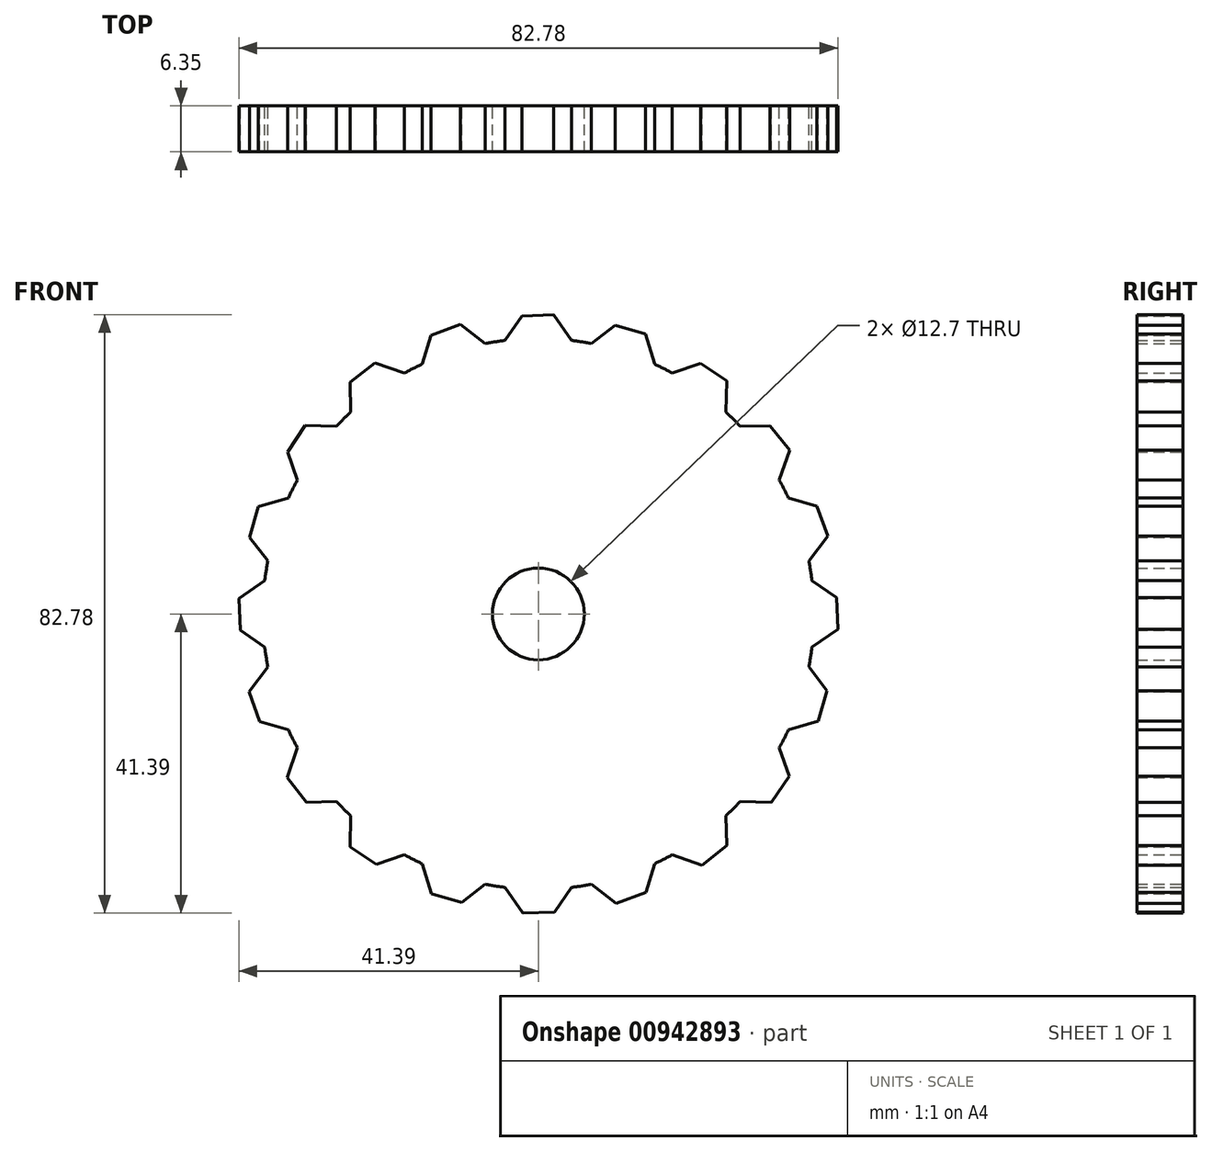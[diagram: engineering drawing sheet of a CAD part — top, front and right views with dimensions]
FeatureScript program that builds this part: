
annotation { "Feature Type Name" : "Feature", "Feature Type Description" : "" }
export const myFeature = defineFeature(function(context is Context, id is Id, definition is map)
    precondition{}
    {
        {
            var Q0;
            Q0=qCreatedBy(makeId("Front.planeOp"),FACE);
            var sketch = newSketch(context, id + "F0", { "sketchPlane" : qUnion([Q0])});
            skCircle(sketch, "E0", {"center": v(0, 0) * mm, "radius": 6.35 * mm});
            skArc(sketch, "E1", {"start": v(-4.6, 37.82) * mm, "mid": v(-5.96, 37.63) * mm, "end": v(-7.32, 37.4) * mm});
            skLineSegment(sketch, "E2", {"start": v(-2.24, 41.21) * mm, "end": v(-4.6, 37.82) * mm});
            skLineSegment(sketch, "E3", {"start": v(2.12, 41.39) * mm, "end": v(4.6, 37.82) * mm});
            skLineSegment(sketch, "E4", {"start": v(-2.24, 41.21) * mm, "end": v(2.12, 41.39) * mm});
            skLineSegment(sketch, "E5.1.0", {"start": v(14.8, 38.7) * mm, "end": v(16.06, 34.55) * mm});
            skLineSegment(sketch, "E5.1.1", {"start": v(10.6, 39.9) * mm, "end": v(7.32, 37.4) * mm});
            skLineSegment(sketch, "E5.2.0", {"start": v(26.04, 32.24) * mm, "end": v(25.95, 27.9) * mm});
            skLineSegment(sketch, "E5.2.1", {"start": v(22.41, 34.66) * mm, "end": v(18.52, 33.3) * mm});
            skLineSegment(sketch, "E5.3.0", {"start": v(34.73, 22.61) * mm, "end": v(33.3, 18.52) * mm});
            skLineSegment(sketch, "E5.3.1", {"start": v(32.03, 26.04) * mm, "end": v(27.9, 25.95) * mm});
            skLineSegment(sketch, "E5.4.0", {"start": v(40.02, 10.77) * mm, "end": v(37.4, 7.32) * mm});
            skLineSegment(sketch, "E5.4.1", {"start": v(38.5, 14.87) * mm, "end": v(34.55, 16.06) * mm});
            skLineSegment(sketch, "E5.5.0", {"start": v(41.39, -2.12) * mm, "end": v(37.82, -4.6) * mm});
            skLineSegment(sketch, "E5.5.1", {"start": v(41.21, 2.24) * mm, "end": v(37.82, 4.6) * mm});
            skLineSegment(sketch, "E5.6.0", {"start": v(38.7, -14.8) * mm, "end": v(34.55, -16.06) * mm});
            skLineSegment(sketch, "E5.6.1", {"start": v(39.9, -10.6) * mm, "end": v(37.4, -7.32) * mm});
            skLineSegment(sketch, "E5.7.0", {"start": v(32.24, -26.04) * mm, "end": v(27.9, -25.95) * mm});
            skLineSegment(sketch, "E5.7.1", {"start": v(34.66, -22.41) * mm, "end": v(33.3, -18.52) * mm});
            skLineSegment(sketch, "E5.8.0", {"start": v(22.61, -34.73) * mm, "end": v(18.52, -33.3) * mm});
            skLineSegment(sketch, "E5.8.1", {"start": v(26.04, -32.03) * mm, "end": v(25.95, -27.9) * mm});
            skLineSegment(sketch, "E5.9.0", {"start": v(10.77, -40.02) * mm, "end": v(7.32, -37.4) * mm});
            skLineSegment(sketch, "E5.9.1", {"start": v(14.87, -38.5) * mm, "end": v(16.06, -34.55) * mm});
            skLineSegment(sketch, "E5.10.1", {"start": v(2.24, -41.21) * mm, "end": v(4.6, -37.82) * mm});
            skLineSegment(sketch, "E6.1.0", {"start": v(-10.77, 40.02) * mm, "end": v(-7.32, 37.4) * mm});
            skLineSegment(sketch, "E6.1.1", {"start": v(-14.87, 38.5) * mm, "end": v(-16.06, 34.55) * mm});
            skLineSegment(sketch, "E6.2.0", {"start": v(-22.61, 34.73) * mm, "end": v(-18.52, 33.3) * mm});
            skLineSegment(sketch, "E6.2.1", {"start": v(-26.04, 32.03) * mm, "end": v(-25.95, 27.9) * mm});
            skLineSegment(sketch, "E6.3.0", {"start": v(-32.24, 26.04) * mm, "end": v(-27.9, 25.95) * mm});
            skLineSegment(sketch, "E6.3.1", {"start": v(-34.66, 22.41) * mm, "end": v(-33.3, 18.52) * mm});
            skLineSegment(sketch, "E6.4.0", {"start": v(-38.7, 14.8) * mm, "end": v(-34.55, 16.06) * mm});
            skLineSegment(sketch, "E6.4.1", {"start": v(-39.9, 10.6) * mm, "end": v(-37.4, 7.32) * mm});
            skLineSegment(sketch, "E6.5.0", {"start": v(-41.39, 2.12) * mm, "end": v(-37.82, 4.6) * mm});
            skLineSegment(sketch, "E6.5.1", {"start": v(-41.21, -2.24) * mm, "end": v(-37.82, -4.6) * mm});
            skLineSegment(sketch, "E6.6.0", {"start": v(-40.02, -10.77) * mm, "end": v(-37.4, -7.32) * mm});
            skLineSegment(sketch, "E6.6.1", {"start": v(-38.5, -14.87) * mm, "end": v(-34.55, -16.06) * mm});
            skLineSegment(sketch, "E6.7.0", {"start": v(-34.73, -22.61) * mm, "end": v(-33.3, -18.52) * mm});
            skLineSegment(sketch, "E6.7.1", {"start": v(-32.03, -26.04) * mm, "end": v(-27.9, -25.95) * mm});
            skLineSegment(sketch, "E6.8.0", {"start": v(-26.04, -32.24) * mm, "end": v(-25.95, -27.9) * mm});
            skLineSegment(sketch, "E6.8.1", {"start": v(-22.41, -34.66) * mm, "end": v(-18.52, -33.3) * mm});
            skLineSegment(sketch, "E6.9.0", {"start": v(-14.8, -38.7) * mm, "end": v(-16.06, -34.55) * mm});
            skLineSegment(sketch, "E6.9.1", {"start": v(-10.6, -39.9) * mm, "end": v(-7.32, -37.4) * mm});
            skLineSegment(sketch, "E6.10.0", {"start": v(-2.12, -41.39) * mm, "end": v(-4.6, -37.82) * mm});
            skLineSegment(sketch, "E7.1.0", {"start": v(-14.87, 38.5) * mm, "end": v(-10.77, 40.02) * mm});
            skLineSegment(sketch, "E7.2.0", {"start": v(-26.04, 32.03) * mm, "end": v(-22.61, 34.73) * mm});
            skLineSegment(sketch, "E7.3.0", {"start": v(-34.66, 22.41) * mm, "end": v(-32.24, 26.04) * mm});
            skLineSegment(sketch, "E7.4.0", {"start": v(-39.9, 10.6) * mm, "end": v(-38.7, 14.8) * mm});
            skLineSegment(sketch, "E7.5.0", {"start": v(-41.21, -2.24) * mm, "end": v(-41.39, 2.12) * mm});
            skLineSegment(sketch, "E7.6.0", {"start": v(-38.5, -14.87) * mm, "end": v(-40.02, -10.77) * mm});
            skLineSegment(sketch, "E7.7.0", {"start": v(-32.03, -26.04) * mm, "end": v(-34.73, -22.61) * mm});
            skLineSegment(sketch, "E7.8.0", {"start": v(-22.41, -34.66) * mm, "end": v(-26.04, -32.24) * mm});
            skLineSegment(sketch, "E7.9.0", {"start": v(-10.6, -39.9) * mm, "end": v(-14.8, -38.7) * mm});
            skLineSegment(sketch, "E7.10.0", {"start": v(2.24, -41.21) * mm, "end": v(-2.12, -41.39) * mm});
            skLineSegment(sketch, "E8.1.0", {"start": v(10.6, 39.9) * mm, "end": v(14.8, 38.7) * mm});
            skLineSegment(sketch, "E8.2.0", {"start": v(22.41, 34.66) * mm, "end": v(26.04, 32.24) * mm});
            skLineSegment(sketch, "E8.3.0", {"start": v(32.03, 26.04) * mm, "end": v(34.73, 22.61) * mm});
            skLineSegment(sketch, "E8.4.0", {"start": v(38.5, 14.87) * mm, "end": v(40.02, 10.77) * mm});
            skLineSegment(sketch, "E8.5.0", {"start": v(41.21, 2.24) * mm, "end": v(41.39, -2.12) * mm});
            skLineSegment(sketch, "E8.6.0", {"start": v(39.9, -10.6) * mm, "end": v(38.7, -14.8) * mm});
            skLineSegment(sketch, "E8.7.0", {"start": v(34.66, -22.41) * mm, "end": v(32.24, -26.04) * mm});
            skLineSegment(sketch, "E8.8.0", {"start": v(26.04, -32.03) * mm, "end": v(22.61, -34.73) * mm});
            skLineSegment(sketch, "E8.9.0", {"start": v(14.87, -38.5) * mm, "end": v(10.77, -40.02) * mm});
            skPoint(sketch, "E9.start.orphan", {"position": v(0, 38.1) * mm});
            skArc(sketch, "E10.trimOffspring", {"start": v(7.32, 37.4) * mm, "mid": v(5.96, 37.63) * mm, "end": v(4.6, 37.82) * mm});
            skArc(sketch, "E11.trimOffspring", {"start": v(18.52, 33.3) * mm, "mid": v(17.3, 33.95) * mm, "end": v(16.06, 34.55) * mm});
            skArc(sketch, "E12.trimOffspring", {"start": v(27.9, 25.95) * mm, "mid": v(26.94, 26.94) * mm, "end": v(25.95, 27.9) * mm});
            skArc(sketch, "E13.trimOffspring", {"start": v(34.55, 16.06) * mm, "mid": v(33.95, 17.3) * mm, "end": v(33.3, 18.52) * mm});
            skArc(sketch, "E14.trimOffspring", {"start": v(37.82, 4.6) * mm, "mid": v(37.63, 5.96) * mm, "end": v(37.4, 7.32) * mm});
            skArc(sketch, "E15.trimOffspring", {"start": v(37.4, -7.32) * mm, "mid": v(37.63, -5.96) * mm, "end": v(37.82, -4.6) * mm});
            skArc(sketch, "E16.trimOffspring", {"start": v(33.3, -18.52) * mm, "mid": v(33.95, -17.3) * mm, "end": v(34.55, -16.06) * mm});
            skArc(sketch, "E17.trimOffspring", {"start": v(25.95, -27.9) * mm, "mid": v(26.94, -26.94) * mm, "end": v(27.9, -25.95) * mm});
            skArc(sketch, "E18.trimOffspring", {"start": v(16.06, -34.55) * mm, "mid": v(17.3, -33.95) * mm, "end": v(18.52, -33.3) * mm});
            skArc(sketch, "E19.trimOffspring", {"start": v(4.6, -37.82) * mm, "mid": v(5.96, -37.63) * mm, "end": v(7.32, -37.4) * mm});
            skArc(sketch, "E20.trimOffspring", {"start": v(-7.32, -37.4) * mm, "mid": v(-5.96, -37.63) * mm, "end": v(-4.6, -37.82) * mm});
            skArc(sketch, "E21.trimOffspring", {"start": v(-18.52, -33.3) * mm, "mid": v(-17.3, -33.95) * mm, "end": v(-16.06, -34.55) * mm});
            skArc(sketch, "E22.trimOffspring", {"start": v(-27.9, -25.95) * mm, "mid": v(-26.94, -26.94) * mm, "end": v(-25.95, -27.9) * mm});
            skArc(sketch, "E23.trimOffspring", {"start": v(-34.55, -16.06) * mm, "mid": v(-33.95, -17.3) * mm, "end": v(-33.3, -18.52) * mm});
            skArc(sketch, "E24.trimOffspring", {"start": v(-37.82, -4.6) * mm, "mid": v(-37.63, -5.96) * mm, "end": v(-37.4, -7.32) * mm});
            skArc(sketch, "E25.trimOffspring", {"start": v(-37.4, 7.32) * mm, "mid": v(-37.63, 5.96) * mm, "end": v(-37.82, 4.6) * mm});
            skArc(sketch, "E26.trimOffspring", {"start": v(-33.3, 18.52) * mm, "mid": v(-33.95, 17.3) * mm, "end": v(-34.55, 16.06) * mm});
            skArc(sketch, "E27.trimOffspring", {"start": v(-25.95, 27.9) * mm, "mid": v(-26.94, 26.94) * mm, "end": v(-27.9, 25.95) * mm});
            skArc(sketch, "E28.trimOffspring", {"start": v(-16.06, 34.55) * mm, "mid": v(-17.3, 33.95) * mm, "end": v(-18.52, 33.3) * mm});
            skPoint(sketch, "E29", {"position": v(-0.06, 41.3) * mm});
            skSolve(sketch);
        }
        {
            var Q0;
            Q0 = qSketchRegion(id + "F0", true);
            extrude(context, id + "F1", {"entities" : qUnion([Q0]), "depth" : 6.35 * mm, "offsetDistance" : 25.4 * mm});
        }
    });
